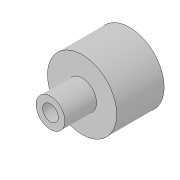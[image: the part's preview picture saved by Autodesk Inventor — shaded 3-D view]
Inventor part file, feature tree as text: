
AUTODESK INVENTOR PART (.ipt)
format: ipt  version: 2018.3 (Build 223284000, 284)  size: 92,672 bytes
history: native  units: in
note: dims shown in document units (in); Inventor stores cm internally (conversion verified against a paired STEP export)
features: extrude x3, sketch x3
ambient origin geometry x8: Origin, YZ Plane, XZ Plane, XY Plane, X Axis, Y Axis, Z Axis, Center Point
bodies: Solid1 (feature_tree)
feature tree (6):
  extrude  "Extrusion1"  Depth=0.5in TaperAngle=0.0deg
  extrude  "Extrusion2"  Depth=0.2in TaperAngle=0.0deg
  extrude  "Extrusion3"  Depth=0.2in TaperAngle=0.0deg
  sketch  "Sketch1"  dims[d0=0.4375in d1=0.5in d2=0.0in]
  sketch  "Sketch2"  dims[d3=0.1825in d4=0.2in d5=0.0in]
  sketch  "Sketch3"  dims[d6=0.0988in d7=0.2in d8=0.0in]
